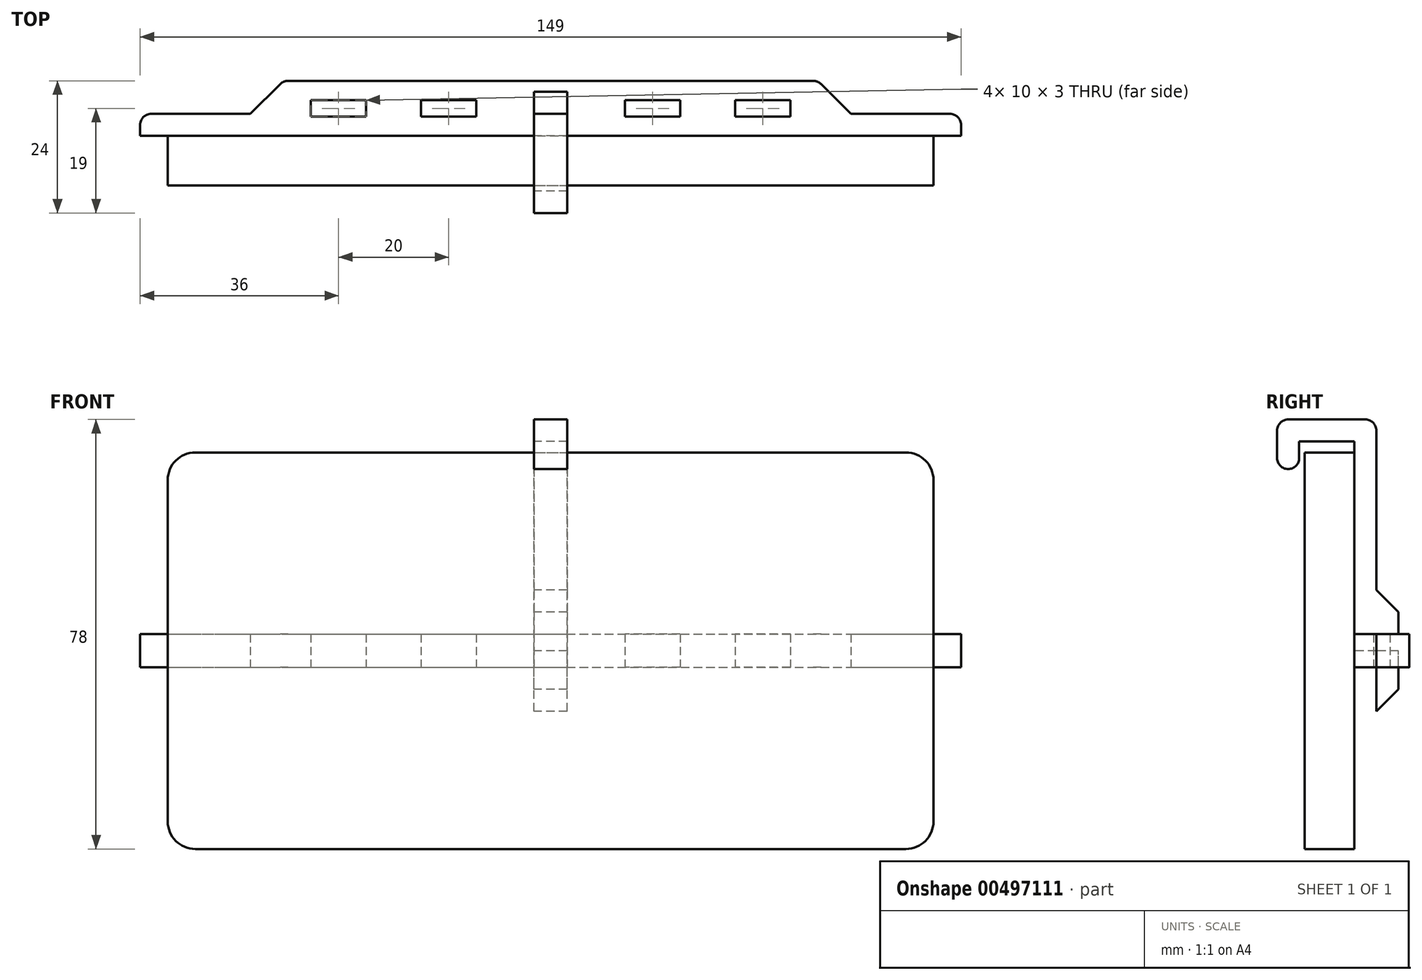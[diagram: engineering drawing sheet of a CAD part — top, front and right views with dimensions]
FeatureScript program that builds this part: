
annotation { "Feature Type Name" : "Feature", "Feature Type Description" : "" }
export const myFeature = defineFeature(function(context is Context, id is Id, definition is map)
    precondition{}
    {
        {
            var Q0;
            Q0=qCreatedBy(makeId("Front.planeOp"),FACE);
            var sketch = newSketch(context, id + "F0", { "sketchPlane" : qUnion([Q0])});
            skLineSegment(sketch, "E0.bottom", {"start": v(-69.5, 36) * mm, "end": v(69.5, 36) * mm});
            skLineSegment(sketch, "E0.top", {"start": v(-69.5, -36) * mm, "end": v(69.5, -36) * mm});
            skLineSegment(sketch, "E0.left", {"start": v(-69.5, 36) * mm, "end": v(-69.5, -36) * mm});
            skLineSegment(sketch, "E0.right", {"start": v(69.5, 36) * mm, "end": v(69.5, -36) * mm});
            skLineSegment(sketch, "E1", {"start": v(-69.5, -36) * mm, "end": v(69.5, 36) * mm, "construction": true});
            skLineSegment(sketch, "E2", {"start": v(69.5, -36) * mm, "end": v(-69.5, 36) * mm, "construction": true});
            skPoint(sketch, "E3", {"position": v(0, 0) * mm});
            skSolve(sketch);
        }
        {
            var Q0;
            Q0=makeQuery(id+"F0.imprint","IMPRINT",FACE,{"disambiguationData":[TD([[makeQuery(id+"F0.imprint","IMPRINT",EDGE,{"derivedFrom":sQuery(id+"F0.wireOp",EDGE,"E0.bottom")}),-1.0]])]});
            extrude(context, id + "F1", {"entities" : qUnion([Q0]), "depth" : 9 * mm});
        }
        {
            var Q0;
            Q0=makeQuery(id+"F1.opExtrude","SWEPT_EDGE",EDGE,{"disambiguationData":[OSD([sQuery(id+"F0.wireOp",EDGE,"E0.bottom"),sQuery(id+"F0.wireOp",EDGE,"E0.left")])]});
            var Q1;
            Q1=makeQuery(id+"F1.opExtrude","SWEPT_EDGE",EDGE,{"disambiguationData":[OSD([sQuery(id+"F0.wireOp",EDGE,"E0.bottom"),sQuery(id+"F0.wireOp",EDGE,"E0.right")])]});
            var Q2;
            Q2=makeQuery(id+"F1.opExtrude","SWEPT_EDGE",EDGE,{"disambiguationData":[OSD([sQuery(id+"F0.wireOp",EDGE,"E0.top"),sQuery(id+"F0.wireOp",EDGE,"E0.right")])]});
            var Q3;
            Q3=makeQuery(id+"F1.opExtrude","SWEPT_EDGE",EDGE,{"disambiguationData":[OSD([sQuery(id+"F0.wireOp",EDGE,"E0.top"),sQuery(id+"F0.wireOp",EDGE,"E0.left")])]});
            fillet(context, id + "F2", {"entities" : qUnion([Q0, Q1, Q2, Q3]), "radius" : 5 * mm, "tangentPropagation" : true, "allowEdgeOverflow" : false});
        }
        {
            var Q0;
            Q0=qCreatedBy(makeId("Top.planeOp"),FACE);
            var sketch = newSketch(context, id + "F3", { "sketchPlane" : qUnion([Q0])});
            skLineSegment(sketch, "E4.bottom", {"start": v(-72.5, 4) * mm, "end": v(72.5, 4) * mm});
            skLineSegment(sketch, "E4.top", {"start": v(-74.5, 0) * mm, "end": v(74.5, 0) * mm});
            skLineSegment(sketch, "E4.left", {"start": v(-74.5, 2) * mm, "end": v(-74.5, 0) * mm});
            skLineSegment(sketch, "E4.right", {"start": v(74.5, 2) * mm, "end": v(74.5, 0) * mm});
            skLineSegment(sketch, "E5.bottom", {"start": v(74.5, 0) * mm, "end": v(70.5, 0) * mm});
            skLineSegment(sketch, "E5.top", {"start": v(72.5, -10) * mm, "end": v(72.5, -10) * mm});
            skLineSegment(sketch, "E5.left", {"start": v(74.5, 0) * mm, "end": v(74.5, -8) * mm});
            skLineSegment(sketch, "E5.right", {"start": v(70.5, 0) * mm, "end": v(70.5, -8) * mm});
            skLineSegment(sketch, "E6.bottom", {"start": v(-74.5, 0) * mm, "end": v(-70.5, 0) * mm});
            skLineSegment(sketch, "E6.top", {"start": v(-72.5, -10) * mm, "end": v(-72.5, -10) * mm});
            skLineSegment(sketch, "E6.left", {"start": v(-74.5, 0) * mm, "end": v(-74.5, -8) * mm});
            skLineSegment(sketch, "E6.right", {"start": v(-70.5, 0) * mm, "end": v(-70.5, -8) * mm});
            skLineSegment(sketch, "E7", {"start": v(-54.5, 4) * mm, "end": v(-49.09, 9.41) * mm});
            skLineSegment(sketch, "E8", {"start": v(-47.67, 10) * mm, "end": v(47.67, 10) * mm});
            skLineSegment(sketch, "E9", {"start": v(49.09, 9.41) * mm, "end": v(54.5, 4) * mm});
            skPoint(sketch, "E10.visualSharp", {"position": v(-74.5, 4) * mm});
            skArc(sketch, "E10.filletArc", {"start": v(-72.5, 4) * mm, "mid": v(-73.91, 3.41) * mm, "end": v(-74.5, 2) * mm});
            skPoint(sketch, "E11.visualSharp", {"position": v(-74.5, -10) * mm});
            skArc(sketch, "E11.filletArc", {"start": v(-74.5, -8) * mm, "mid": v(-73.91, -9.41) * mm, "end": v(-72.5, -10) * mm});
            skPoint(sketch, "E12.visualSharp", {"position": v(-70.5, -10) * mm});
            skArc(sketch, "E12.filletArc", {"start": v(-72.5, -10) * mm, "mid": v(-71.09, -9.41) * mm, "end": v(-70.5, -8) * mm});
            skPoint(sketch, "E13.visualSharp", {"position": v(70.5, -10) * mm});
            skArc(sketch, "E13.filletArc", {"start": v(70.5, -8) * mm, "mid": v(71.09, -9.41) * mm, "end": v(72.5, -10) * mm});
            skPoint(sketch, "E14.visualSharp", {"position": v(74.5, -10) * mm});
            skArc(sketch, "E14.filletArc", {"start": v(72.5, -10) * mm, "mid": v(73.91, -9.41) * mm, "end": v(74.5, -8) * mm});
            skPoint(sketch, "E15.visualSharp", {"position": v(74.5, 4) * mm});
            skArc(sketch, "E15.filletArc", {"start": v(74.5, 2) * mm, "mid": v(73.91, 3.41) * mm, "end": v(72.5, 4) * mm});
            skLineSegment(sketch, "E16.bottom", {"start": v(-43.5, 6.5) * mm, "end": v(-33.5, 6.5) * mm});
            skLineSegment(sketch, "E16.top", {"start": v(-43.5, 3.5) * mm, "end": v(-33.5, 3.5) * mm});
            skLineSegment(sketch, "E16.left", {"start": v(-43.5, 6.5) * mm, "end": v(-43.5, 3.5) * mm});
            skLineSegment(sketch, "E16.right", {"start": v(-33.5, 6.5) * mm, "end": v(-33.5, 3.5) * mm});
            skLineSegment(sketch, "E17.bottom", {"start": v(-23.5, 6.5) * mm, "end": v(-13.5, 6.5) * mm});
            skLineSegment(sketch, "E17.top", {"start": v(-23.5, 3.5) * mm, "end": v(-13.5, 3.5) * mm});
            skLineSegment(sketch, "E17.left", {"start": v(-23.5, 6.5) * mm, "end": v(-23.5, 3.5) * mm});
            skLineSegment(sketch, "E17.right", {"start": v(-13.5, 6.5) * mm, "end": v(-13.5, 3.5) * mm});
            skLineSegment(sketch, "E18", {"start": v(0, 10) * mm, "end": v(0, 4) * mm});
            skLineSegment(sketch, "E19.MirrorCS", {"start": v(13.5, 6.5) * mm, "end": v(13.5, 3.5) * mm});
            skLineSegment(sketch, "E20.MirrorCS", {"start": v(23.5, 3.5) * mm, "end": v(13.5, 3.5) * mm});
            skLineSegment(sketch, "E21.MirrorCS", {"start": v(23.5, 6.5) * mm, "end": v(13.5, 6.5) * mm});
            skLineSegment(sketch, "E22.MirrorCS", {"start": v(23.5, 6.5) * mm, "end": v(23.5, 3.5) * mm});
            skLineSegment(sketch, "E23.MirrorCS", {"start": v(33.5, 6.5) * mm, "end": v(33.5, 3.5) * mm});
            skLineSegment(sketch, "E24.MirrorCS", {"start": v(43.5, 6.5) * mm, "end": v(33.5, 6.5) * mm});
            skLineSegment(sketch, "E25.MirrorCS", {"start": v(43.5, 6.5) * mm, "end": v(43.5, 3.5) * mm});
            skLineSegment(sketch, "E26.MirrorCS", {"start": v(43.5, 3.5) * mm, "end": v(33.5, 3.5) * mm});
            skPoint(sketch, "E27.visualSharp", {"position": v(-48.5, 10) * mm});
            skArc(sketch, "E27.filletArc", {"start": v(-47.67, 10) * mm, "mid": v(-48.44, 9.85) * mm, "end": v(-49.09, 9.41) * mm});
            skPoint(sketch, "E28.visualSharp", {"position": v(48.5, 10) * mm});
            skArc(sketch, "E28.filletArc", {"start": v(49.09, 9.41) * mm, "mid": v(48.44, 9.85) * mm, "end": v(47.67, 10) * mm});
            skLineSegment(sketch, "E29.bottom", {"start": v(3, 0) * mm, "end": v(-3, 0) * mm});
            skLineSegment(sketch, "E29.top", {"start": v(3, 4) * mm, "end": v(-3, 4) * mm});
            skLineSegment(sketch, "E29.left", {"start": v(3, 0) * mm, "end": v(3, 4) * mm});
            skLineSegment(sketch, "E29.right", {"start": v(-3, 0) * mm, "end": v(-3, 4) * mm});
            skSolve(sketch);
        }
        {
            var Q0;
            Q0=makeQuery(id+"F3.imprint","IMPRINT",FACE,{"disambiguationData":[TD([[makeQuery(id+"F3.imprint","IMPRINT",EDGE,{"derivedFrom":sQuery(id+"F3.wireOp",EDGE,"E4.top")}),1.0]])]});
            var Q1;
            Q1=makeQuery(id+"F3.imprint","IMPRINT",FACE,{"disambiguationData":[TD([[makeQuery(id+"F3.imprint","IMPRINT",EDGE,{"derivedFrom":sQuery(id+"F3.wireOp",EDGE,"E6.bottom")}),-1.0]])]});
            var Q2;
            Q2=makeQuery(id+"F3.imprint","IMPRINT",FACE,{"disambiguationData":[TD([[makeQuery(id+"F3.imprint","IMPRINT",EDGE,{"derivedFrom":sQuery(id+"F3.wireOp",EDGE,"E5.bottom")}),1.0]])]});
            var Q3;
            {var subQ4=sQuery(id+"F3.wireOp",EDGE,"E9");Q3=makeQuery(id+"F3.imprint","IMPRINT",FACE,{"disambiguationData":[TD([[makeQuery(id+"F3.imprint","IMPRINT",EDGE,{"derivedFrom":subQ4}),-1.0]])]});}
            var Q4;
            {var subQ12=sQuery(id+"F3.wireOp",EDGE,"E7");Q4=makeQuery(id+"F3.imprint","IMPRINT",FACE,{"disambiguationData":[TD([[makeQuery(id+"F3.imprint","IMPRINT",EDGE,{"derivedFrom":subQ12}),-1.0]])]});}
            extrude(context, id + "F4", {"entities" : qUnion([Q0, Q1, Q2, Q3, Q4]), "endBound" : BoundingType.SYMMETRIC, "depth" : 6 * mm});
        }
        {
            var Q0;
            Q0=qCreatedBy(makeId("Right.planeOp"),FACE);
            var sketch = newSketch(context, id + "F5", { "sketchPlane" : qUnion([Q0])});
            skLineSegment(sketch, "E30", {"start": v(0, 38) * mm, "end": v(-10, 38) * mm});
            skLineSegment(sketch, "E31", {"start": v(-10, 38) * mm, "end": v(-10, 35) * mm});
            skLineSegment(sketch, "E32", {"start": v(-12, 33) * mm, "end": v(-12, 33) * mm});
            skLineSegment(sketch, "E33", {"start": v(-14, 35) * mm, "end": v(-14, 40) * mm});
            skLineSegment(sketch, "E34", {"start": v(-12, 42) * mm, "end": v(2, 42) * mm});
            skLineSegment(sketch, "E35", {"start": v(4, 40) * mm, "end": v(4, 0) * mm});
            skLineSegment(sketch, "E36", {"start": v(4, 0) * mm, "end": v(0, 0) * mm});
            skLineSegment(sketch, "E37", {"start": v(0, 0) * mm, "end": v(0, 38) * mm});
            skPoint(sketch, "E38.visualSharp", {"position": v(-10, 33) * mm});
            skArc(sketch, "E38.filletArc", {"start": v(-12, 33) * mm, "mid": v(-10.59, 33.59) * mm, "end": v(-10, 35) * mm});
            skPoint(sketch, "E39.visualSharp", {"position": v(-14, 33) * mm});
            skArc(sketch, "E39.filletArc", {"start": v(-14, 35) * mm, "mid": v(-13.41, 33.59) * mm, "end": v(-12, 33) * mm});
            skPoint(sketch, "E40.visualSharp", {"position": v(-14, 42) * mm});
            skArc(sketch, "E40.filletArc", {"start": v(-12, 42) * mm, "mid": v(-13.41, 41.41) * mm, "end": v(-14, 40) * mm});
            skPoint(sketch, "E41.visualSharp", {"position": v(4, 42) * mm});
            skArc(sketch, "E41.filletArc", {"start": v(4, 40) * mm, "mid": v(3.41, 41.41) * mm, "end": v(2, 42) * mm});
            skLineSegment(sketch, "E42", {"start": v(4, 11) * mm, "end": v(8, 7) * mm});
            skLineSegment(sketch, "E43", {"start": v(8, 7) * mm, "end": v(8, 0) * mm});
            skLineSegment(sketch, "E44", {"start": v(8, 0) * mm, "end": v(4, 0) * mm});
            skArc(sketch, "E45.MirrorCS", {"start": v(-12, -33) * mm, "mid": v(-10.59, -33.59) * mm, "end": v(-10, -35) * mm});
            skLineSegment(sketch, "E46.MirrorCS", {"start": v(-10, -38) * mm, "end": v(-10, -35) * mm});
            skArc(sketch, "E47.MirrorCS", {"start": v(4, -40) * mm, "mid": v(3.41, -41.41) * mm, "end": v(2, -42) * mm});
            skArc(sketch, "E48.MirrorCS", {"start": v(-14, -35) * mm, "mid": v(-13.41, -33.59) * mm, "end": v(-12, -33) * mm});
            skArc(sketch, "E49.MirrorCS", {"start": v(-12, -42) * mm, "mid": v(-13.41, -41.41) * mm, "end": v(-14, -40) * mm});
            skLineSegment(sketch, "E50.MirrorCS", {"start": v(-12, -33) * mm, "end": v(-12, -33) * mm});
            skLineSegment(sketch, "E51.MirrorCS", {"start": v(0, -38) * mm, "end": v(-10, -38) * mm});
            skLineSegment(sketch, "E52.MirrorCS", {"start": v(-14, -35) * mm, "end": v(-14, -40) * mm});
            skLineSegment(sketch, "E53.MirrorCS", {"start": v(-12, -42) * mm, "end": v(2, -42) * mm});
            skLineSegment(sketch, "E54.MirrorCS", {"start": v(0, 0) * mm, "end": v(0, -38) * mm});
            skLineSegment(sketch, "E55.MirrorCS", {"start": v(8, -7) * mm, "end": v(8, 0) * mm});
            skLineSegment(sketch, "E56.MirrorCS", {"start": v(4, -11) * mm, "end": v(8, -7) * mm});
            skPoint(sketch, "E57.MirrorP", {"position": v(-14, -42) * mm});
            skPoint(sketch, "E58.MirrorP", {"position": v(-14, -33) * mm});
            skPoint(sketch, "E59.MirrorP", {"position": v(4, -42) * mm});
            skLineSegment(sketch, "E60.MirrorCS", {"start": v(4, -40) * mm, "end": v(4, 0) * mm});
            skPoint(sketch, "E61.MirrorP", {"position": v(-10, -33) * mm});
            skLineSegment(sketch, "E62.left", {"start": v(4, 3) * mm, "end": v(4, -3) * mm});
            skLineSegment(sketch, "E63.bottom", {"start": v(4, 3) * mm, "end": v(8, 3) * mm});
            skLineSegment(sketch, "E63.top", {"start": v(4, -3) * mm, "end": v(8, -3) * mm});
            skLineSegment(sketch, "E63.right", {"start": v(8, 3) * mm, "end": v(8, -3) * mm});
            skSolve(sketch);
        }
        {
            var Q0;
            {var subQ2=sQuery(id+"F5.wireOp",EDGE,"E42");Q0=makeQuery(id+"F5.imprint","IMPRINT",FACE,{"disambiguationData":[TD([[makeQuery(id+"F5.imprint","IMPRINT",EDGE,{"derivedFrom":subQ2}),-1.0]])]});}
            var Q1;
            Q1=makeQuery(id+"F5.imprint","IMPRINT",FACE,{"disambiguationData":[TD([[makeQuery(id+"F5.imprint","IMPRINT",EDGE,{"derivedFrom":sQuery(id+"F5.wireOp",EDGE,"E30")}),-1.0]])]});
            var Q2;
            Q2=makeQuery(id+"F5.imprint","IMPRINT",FACE,{"disambiguationData":[TD([[makeQuery(id+"F5.imprint","IMPRINT",EDGE,{"derivedFrom":sQuery(id+"F5.wireOp",EDGE,"E45.MirrorCS")}),-1.0]])]});
            var Q3;
            Q3=makeQuery(id+"F5.imprint","IMPRINT",FACE,{"disambiguationData":[TD([[makeQuery(id+"F5.imprint","IMPRINT",EDGE,{"derivedFrom":sQuery(id+"F5.wireOp",EDGE,"E55.MirrorCS")}),1.0]])]});
            extrude(context, id + "F6", {"entities" : qUnion([Q0, Q1, Q2, Q3]), "endBound" : BoundingType.SYMMETRIC, "depth" : 6 * mm});
        }
    });
